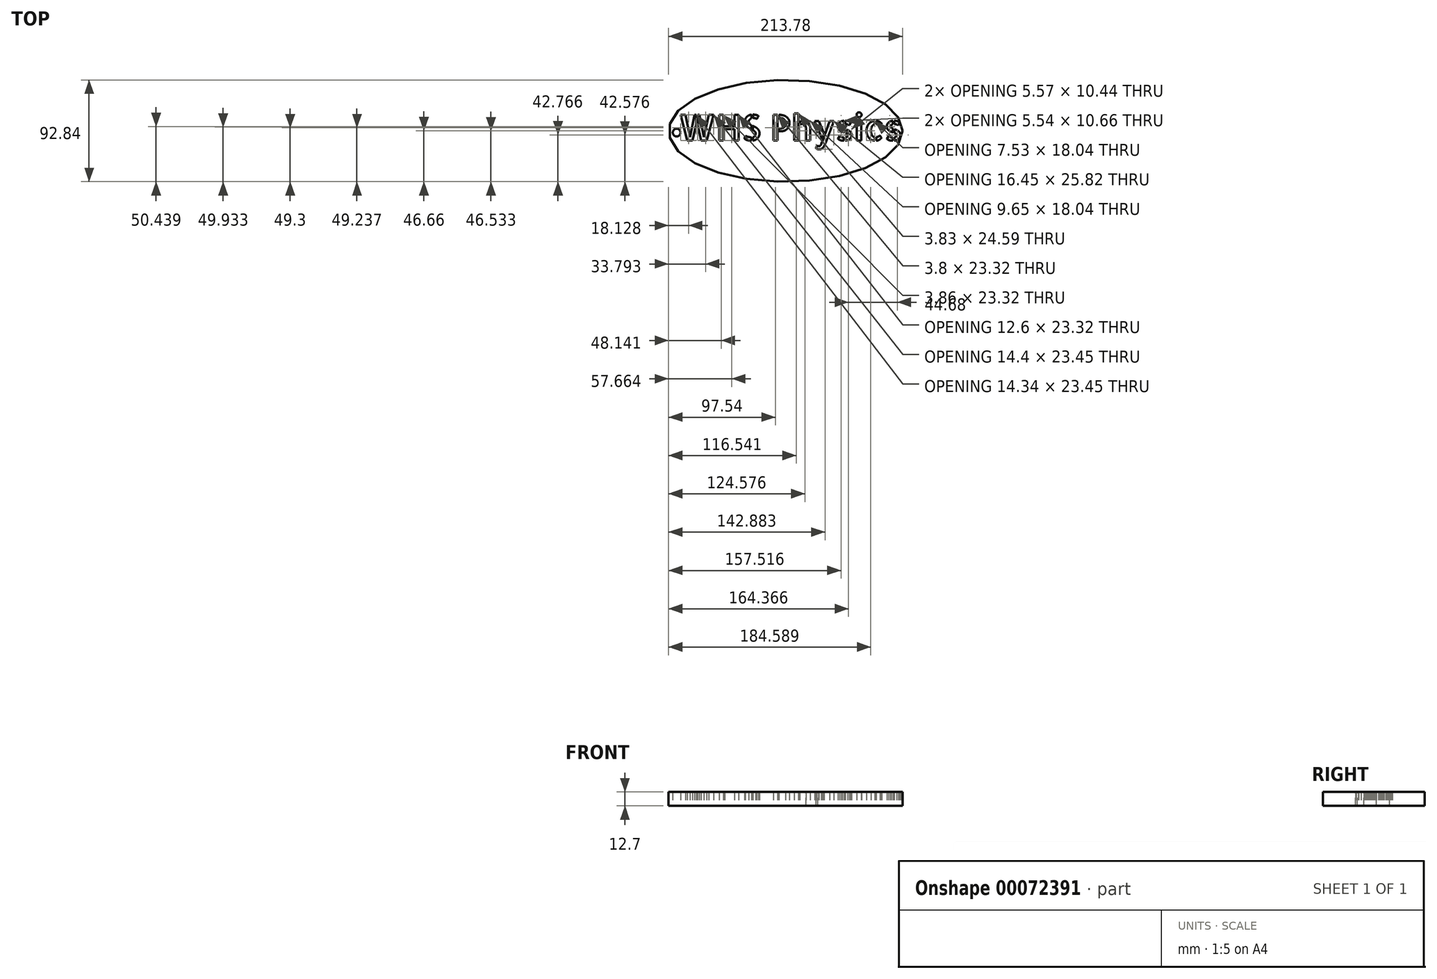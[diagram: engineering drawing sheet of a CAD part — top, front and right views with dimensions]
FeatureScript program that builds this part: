
annotation { "Feature Type Name" : "Feature", "Feature Type Description" : "" }
export const myFeature = defineFeature(function(context is Context, id is Id, definition is map)
    precondition{}
    {
        {
            var Q0;
            Q0=qCreatedBy(makeId("Top.planeOp"),FACE);
            var sketch = newSketch(context, id + "F0", { "sketchPlane" : qUnion([Q0])});
            skEllipse(sketch, "E0", {"center": v(0, 0) * mm, "majorRadius": 106.89 * mm, "minorRadius": 46.42 * mm, "majorAxis": v(1, 0)});
            skText(sketch, "E1", { "text": "WHS Physics", "fontName": "AllertaStencil-Regular.ttf"});
            skCircle(sketch, "E2", {"center": v(-99.58, -1.54) * mm, "radius": 3.52 * mm});
            skPoint(sketch, "E2.first.point", {"position": v(-102.75, 0) * mm});
            skPoint(sketch, "E2.first.point.positionSnap0", {"position": v(-106.89, 0) * mm});
            skPoint(sketch, "E2.second.point", {"position": v(-101.51, -4.49) * mm});
            skPoint(sketch, "E2.third.point", {"position": v(-98.24, -4.8) * mm});
            const initialGuessF0  = {"E1": [-0.09824, -0.00878, 1, 0, 0.02333]};
            skSetInitialGuess(sketch, initialGuessF0);
            skSolve(sketch);
        }
        {
            var Q0;
            Q0 = qSketchRegion(id + "F0", true);
            extrude(context, id + "F1", {"entities" : qUnion([Q0]), "endBound" : BoundingType.SYMMETRIC, "depth" : 12.7 * mm});
        }
    });
